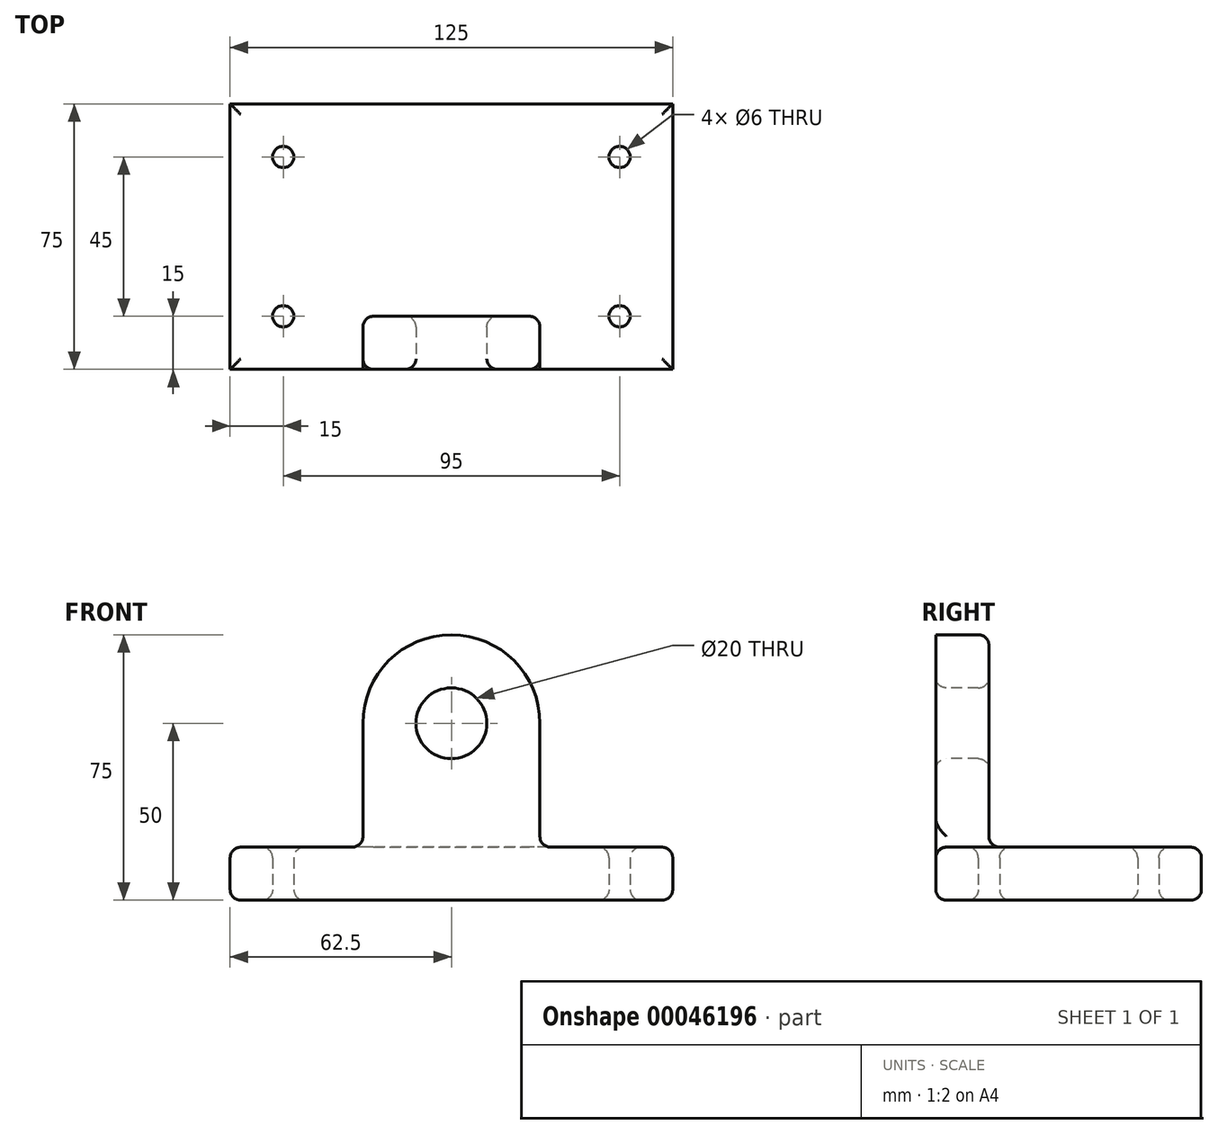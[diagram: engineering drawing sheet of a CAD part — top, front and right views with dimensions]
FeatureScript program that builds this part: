
annotation { "Feature Type Name" : "Feature", "Feature Type Description" : "" }
export const myFeature = defineFeature(function(context is Context, id is Id, definition is map)
    precondition{}
    {
        {
            var Q0;
            Q0=qCreatedBy(makeId("Top.planeOp"),FACE);
            var sketch = newSketch(context, id + "F0", { "sketchPlane" : qUnion([Q0])});
            skLineSegment(sketch, "E0.rect.bottom", {"start": v(62.5, 37.5) * mm, "end": v(-62.5, 37.5) * mm});
            skLineSegment(sketch, "E0.rect.top", {"start": v(62.5, -37.5) * mm, "end": v(-62.5, -37.5) * mm});
            skLineSegment(sketch, "E0.rect.left", {"start": v(62.5, 37.5) * mm, "end": v(62.5, -37.5) * mm});
            skLineSegment(sketch, "E0.rect.right", {"start": v(-62.5, 37.5) * mm, "end": v(-62.5, -37.5) * mm});
            skPoint(sketch, "E0.rect.middle", {"position": v(0, 0) * mm});
            skLineSegment(sketch, "E1.rect.bottom", {"start": v(47.5, 22.5) * mm, "end": v(-47.5, 22.5) * mm, "construction": true});
            skLineSegment(sketch, "E1.rect.top", {"start": v(47.5, -22.5) * mm, "end": v(-47.5, -22.5) * mm, "construction": true});
            skLineSegment(sketch, "E1.rect.left", {"start": v(47.5, 22.5) * mm, "end": v(47.5, -22.5) * mm, "construction": true});
            skLineSegment(sketch, "E1.rect.right", {"start": v(-47.5, 22.5) * mm, "end": v(-47.5, -22.5) * mm, "construction": true});
            skCircle(sketch, "E2", {"center": v(-47.5, 22.5) * mm, "radius": 3 * mm});
            skCircle(sketch, "E3", {"center": v(47.5, 22.5) * mm, "radius": 3 * mm});
            skCircle(sketch, "E4", {"center": v(47.5, -22.5) * mm, "radius": 3 * mm});
            skCircle(sketch, "E5", {"center": v(-47.5, -22.5) * mm, "radius": 3 * mm});
            skSolve(sketch);
        }
        {
            var Q0;
            Q0=makeQuery(id+"F0.imprint","IMPRINT",FACE,{"disambiguationData":[TD([[makeQuery(id+"F0.imprint","IMPRINT",EDGE,{"derivedFrom":sQuery(id+"F0.wireOp",EDGE,"E0.rect.bottom")}),1.0]])]});
            extrude(context, id + "F1", {"entities" : qUnion([Q0]), "depth" : 15 * mm});
        }
        {
            var Q0;
            Q0=makeQuery(id+"F1.opExtrude","SWEPT_FACE",FACE,{"disambiguationData":[OSD([sQuery(id+"F0.wireOp",EDGE,"E0.rect.top")])]});
            var sketch = newSketch(context, id + "F2", { "sketchPlane" : qUnion([Q0])});
            skLineSegment(sketch, "E6", {"start": v(0, 0) * mm, "end": v(0, 50) * mm, "construction": true});
            skPoint(sketch, "E6.endSnap0", {"position": v(0, 15) * mm});
            skCircle(sketch, "E7", {"center": v(0, 50) * mm, "radius": 25 * mm});
            skLineSegment(sketch, "E8.bottom", {"start": v(-25, 50) * mm, "end": v(25, 50) * mm});
            skLineSegment(sketch, "E8.top", {"start": v(-25, 0) * mm, "end": v(25, 0) * mm});
            skLineSegment(sketch, "E8.left", {"start": v(-25, 50) * mm, "end": v(-25, 0) * mm});
            skLineSegment(sketch, "E8.right", {"start": v(25, 50) * mm, "end": v(25, 0) * mm});
            skCircle(sketch, "E9", {"center": v(0, 50) * mm, "radius": 10 * mm});
            skSolve(sketch);
        }
        {
            var Q0;
            {var subQ0=sQuery(id+"F2.wireOp",EDGE,"E8.bottom");var subQ1=sQuery(id+"F2.wireOp",EDGE,"E9");var subQ5=makeQuery(id+"F2.imprint","INTERSECT",VERTEX,{"disambiguationData":[OD(0.0)],"derivedFrom":[subQ0,subQ1]});Q0=makeQuery(id+"F2.imprint","IMPRINT",FACE,{"disambiguationData":[TD([[makeQuery(id+"F2.imprint","IMPRINT",EDGE,{"disambiguationData":[TD([[subQ5,1.0]])],"derivedFrom":subQ1}),-1.0]])]});}
            var Q1;
            {var subQ0=sQuery(id+"F2.wireOp",EDGE,"E8.bottom");var subQ1=sQuery(id+"F2.wireOp",EDGE,"E9");var subQ5=makeQuery(id+"F2.imprint","INTERSECT",VERTEX,{"disambiguationData":[OD(0.0)],"derivedFrom":[subQ0,subQ1]});Q1=makeQuery(id+"F2.imprint","IMPRINT",FACE,{"disambiguationData":[TD([[makeQuery(id+"F2.imprint","IMPRINT",EDGE,{"disambiguationData":[TD([[subQ5,-1.0]])],"derivedFrom":subQ1}),-1.0]])]});}
            var Q2;
            {var subQ0=sQuery(id+"F2.wireOp",EDGE,"E8.left");var subQ1=makeQuery(id+"F1.opExtrude","CAP_EDGE",EDGE,{"disambiguationData":[OSD([sQuery(id+"F0.wireOp",EDGE,"E0.rect.top")])],"isStart":false});var subQ2=makeQuery(id+"F2.imprint","INTERSECT",VERTEX,{"derivedFrom":[subQ1,subQ0]});Q2=makeQuery(id+"F2.imprint","IMPRINT",FACE,{"disambiguationData":[TD([[makeQuery(id+"F2.imprint","IMPRINT",EDGE,{"disambiguationData":[TD([[subQ2,1.0]])],"derivedFrom":subQ1}),-1.0]])]});}
            var Q3;
            {var subQ7=sQuery(id+"F2.wireOp",EDGE,"E8.top");Q3=makeQuery(id+"F2.imprint","IMPRINT",FACE,{"disambiguationData":[TD([[makeQuery(id+"F2.imprint","IMPRINT",EDGE,{"derivedFrom":subQ7}),-1.0]])]});}
            extrude(context, id + "F3", {"entities" : qUnion([Q0, Q1, Q2, Q3]), "operationType" : NewBodyOperationType.ADD, "oppositeDirection" : true, "depth" : 15 * mm});
        }
        {
            var Q0;
            Q0=makeQuery(id+"F1.opExtrude","CAP_FACE",FACE,{"disambiguationData":[OSD([sQuery(id+"F0.wireOp",EDGE,"E0.rect.bottom"),sQuery(id+"F0.wireOp",EDGE,"E0.rect.top"),sQuery(id+"F0.wireOp",EDGE,"E0.rect.left"),sQuery(id+"F0.wireOp",EDGE,"E0.rect.right"),sQuery(id+"F0.wireOp",EDGE,"E2"),sQuery(id+"F0.wireOp",EDGE,"E3"),sQuery(id+"F0.wireOp",EDGE,"E4"),sQuery(id+"F0.wireOp",EDGE,"E5")])],"isStart":false});
            var Q1;
            Q1=makeQuery(id+"F3.opExtrude","SWEPT_FACE",FACE,{"disambiguationData":[OSD([sQuery(id+"F2.wireOp",EDGE,"E9")])]});
            var Q2;
            Q2=makeQuery(id+"F3.opExtrude","CAP_EDGE",EDGE,{"disambiguationData":[OSD([sQuery(id+"F2.wireOp",EDGE,"E8.right")])],"isStart":false});
            var Q3;
            Q3=makeQuery(id+"F3.opExtrude","CAP_EDGE",EDGE,{"disambiguationData":[OSD([sQuery(id+"F2.wireOp",EDGE,"E7")])],"isStart":false});
            var Q4;
            Q4=makeQuery(id+"F1.opExtrude","CAP_FACE",FACE,{"disambiguationData":[OSD([sQuery(id+"F0.wireOp",EDGE,"E0.rect.bottom"),sQuery(id+"F0.wireOp",EDGE,"E0.rect.top"),sQuery(id+"F0.wireOp",EDGE,"E0.rect.left"),sQuery(id+"F0.wireOp",EDGE,"E0.rect.right"),sQuery(id+"F0.wireOp",EDGE,"E2"),sQuery(id+"F0.wireOp",EDGE,"E3"),sQuery(id+"F0.wireOp",EDGE,"E4"),sQuery(id+"F0.wireOp",EDGE,"E5")])],"isStart":true});
            fillet(context, id + "F4", {"entities" : qUnion([Q0, Q1, Q2, Q3, Q4]), "radius" : 3 * mm, "tangentPropagation" : true, "allowEdgeOverflow" : false});
        }
    });
